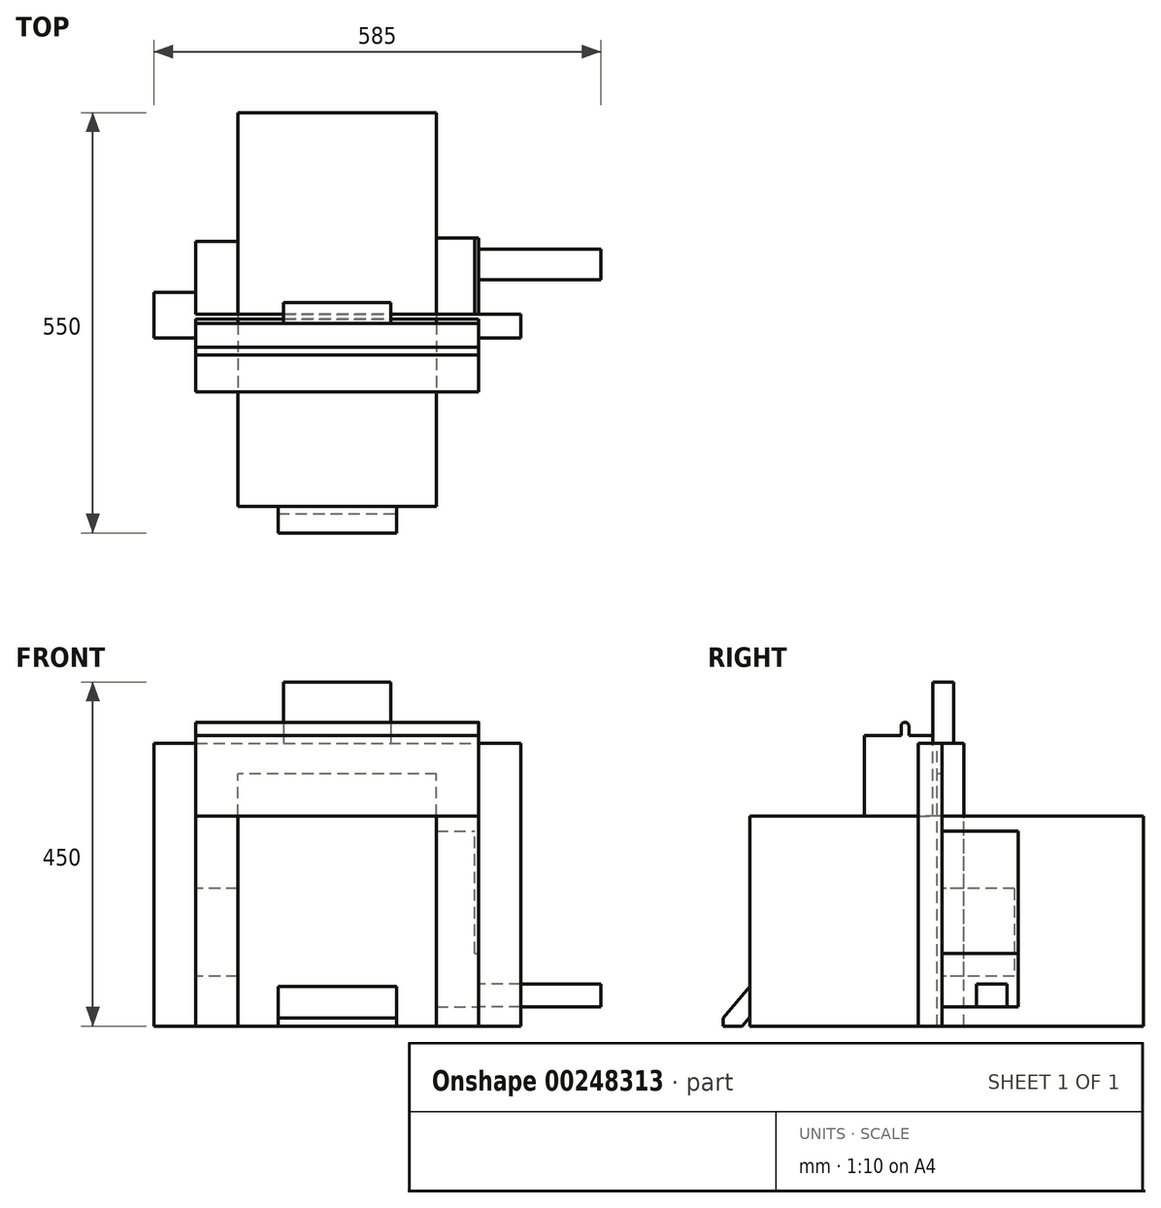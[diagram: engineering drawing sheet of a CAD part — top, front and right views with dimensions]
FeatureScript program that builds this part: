
annotation { "Feature Type Name" : "Feature", "Feature Type Description" : "" }
export const myFeature = defineFeature(function(context is Context, id is Id, definition is map)
    precondition{}
    {
        {
            var Q0;
            Q0=qCreatedBy(makeId("Front.planeOp"),FACE);
            var sketch = newSketch(context, id + "F0", { "sketchPlane" : qUnion([Q0])});
            skLineSegment(sketch, "E0.bottom", {"start": v(-77.5, 0) * mm, "end": v(77.5, 0) * mm});
            skLineSegment(sketch, "E0.top", {"start": v(-77.5, 52) * mm, "end": v(77.5, 52) * mm});
            skLineSegment(sketch, "E0.left", {"start": v(-77.5, 0) * mm, "end": v(-77.5, 52) * mm});
            skLineSegment(sketch, "E0.right", {"start": v(77.5, 0) * mm, "end": v(77.5, 52) * mm});
            skLineSegment(sketch, "E1", {"start": v(0, 0) * mm, "end": v(0, 105.65) * mm, "construction": true});
            skSolve(sketch);
        }
        {
            var Q0;
            Q0 = qSketchRegion(id + "F0", true);
            extrude(context, id + "F1", {"entities" : qUnion([Q0]), "oppositeDirection" : true, "depth" : 65 * mm});
        }
        {
            var Q0;
            Q0=makeQuery(id+"F1.opExtrude","CAP_EDGE",EDGE,{"disambiguationData":[OSD([sQuery(id+"F0.wireOp",EDGE,"E0.top")])],"isStart":true});
            chamfer(context, id + "F2", {"entities" : qUnion([Q0]), "chamferType" : ChamferType.OFFSET_ANGLE, "width" : 35 * mm, "oppositeDirection" : false, "angle" : 50 * degree, "tangentPropagation" : true});
        }
        {
            var Q0;
            Q0=makeQuery(id+"F1.opExtrude","CAP_EDGE",EDGE,{"disambiguationData":[OSD([sQuery(id+"F0.wireOp",EDGE,"E0.bottom")])],"isStart":false});
            chamfer(context, id + "F3", {"entities" : qUnion([Q0]), "chamferType" : ChamferType.OFFSET_ANGLE, "width" : 40 * mm, "oppositeDirection" : false, "angle" : 50 * degree, "tangentPropagation" : true});
        }
        {
            var Q0;
            Q0=makeQuery(id+"F1.opExtrude","SWEPT_FACE",FACE,{"disambiguationData":[OSD([sQuery(id+"F0.wireOp",EDGE,"E0.left")])]});
            var sketch = newSketch(context, id + "F4", { "sketchPlane" : qUnion([Q0])});
            skLineSegment(sketch, "E2.bottom", {"start": v(-35, 52) * mm, "end": v(-95.44, 52) * mm});
            skLineSegment(sketch, "E2.top", {"start": v(-35, 0) * mm, "end": v(-95.44, 0) * mm});
            skLineSegment(sketch, "E2.left", {"start": v(-35, 52) * mm, "end": v(-35, 0) * mm});
            skLineSegment(sketch, "E2.right", {"start": v(-95.44, 52) * mm, "end": v(-95.44, 0) * mm});
            skSolve(sketch);
        }
        {
            var Q0;
            Q0 = qSketchRegion(id + "F4", true);
            extrude(context, id + "F5", {"entities" : qUnion([Q0]), "operationType" : NewBodyOperationType.REMOVE, "endBound" : BoundingType.THROUGH_ALL, "oppositeDirection" : true, "depth" : 25 * mm});
        }
        {
            var Q0;
            Q0=makeQuery(id+"F5.boolean.opBoolean","COPY",FACE,{"derivedFrom":makeQuery(id+"F5.opExtrude","SWEPT_FACE",FACE,{"disambiguationData":[OSD([sQuery(id+"F4.wireOp",EDGE,"E2.left")])]})});
            var sketch = newSketch(context, id + "F6", { "sketchPlane" : qUnion([Q0])});
            skLineSegment(sketch, "E3", {"start": v(0, 0) * mm, "end": v(0, 207.2) * mm, "construction": true});
            skLineSegment(sketch, "E4.bottom", {"start": v(130, 0) * mm, "end": v(-130, 0) * mm});
            skLineSegment(sketch, "E4.top", {"start": v(130, 75) * mm, "end": v(-130, 75) * mm});
            skLineSegment(sketch, "E4.left", {"start": v(130, 0) * mm, "end": v(130, 75) * mm});
            skLineSegment(sketch, "E4.right", {"start": v(-130, 0) * mm, "end": v(-130, 75) * mm});
            skSolve(sketch);
        }
        {
            var Q0;
            Q0 = qSketchRegion(id + "F6", true);
            extrude(context, id + "F7", {"entities" : qUnion([Q0]), "operationType" : NewBodyOperationType.ADD, "depth" : (200 + 235) * mm});
        }
        {
            var Q0;
            Q0=makeQuery(id+"F7.opExtrude","SWEPT_FACE",FACE,{"disambiguationData":[OSD([sQuery(id+"F6.wireOp",EDGE,"E4.left")])]});
            var sketch = newSketch(context, id + "F8", { "sketchPlane" : qUnion([Q0])});
            skLineSegment(sketch, "E5.0", {"start": v(-280, 0) * mm, "end": v(-280, 370) * mm});
            skLineSegment(sketch, "E6.0", {"start": v(-286.3, 0) * mm, "end": v(-286.3, 370) * mm});
            skLineSegment(sketch, "E7", {"start": v(-286.3, 370) * mm, "end": v(-280, 370) * mm});
            skLineSegment(sketch, "E8", {"start": v(-280, 0) * mm, "end": v(-286.3, 0) * mm});
            skSolve(sketch);
        }
        {
            var Q0;
            Q0 = qSketchRegion(id + "F8", true);
            extrude(context, id + "F9", {"entities" : qUnion([Q0]), "operationType" : NewBodyOperationType.ADD, "depth" : 55 * mm});
        }
        {
            var Q0;
            Q0=makeQuery(id+"F9.opExtrude","CAP_FACE",FACE,{"disambiguationData":[OSD([sQuery(id+"F8.wireOp",EDGE,"E5.0"),sQuery(id+"F8.wireOp",EDGE,"E6.0"),sQuery(id+"F8.wireOp",EDGE,"E7"),sQuery(id+"F8.wireOp",EDGE,"E8")])],"isStart":true});
            var sketch = newSketch(context, id + "F10", { "sketchPlane" : qUnion([Q0])});
            skLineSegment(sketch, "E9.0", {"start": v(286.3, 370) * mm, "end": v(280, 370) * mm});
            skLineSegment(sketch, "E10.0", {"start": v(286.3, 329.7) * mm, "end": v(280, 329.7) * mm});
            skLineSegment(sketch, "E11", {"start": v(280, 370) * mm, "end": v(280, 329.7) * mm});
            skLineSegment(sketch, "E12", {"start": v(286.3, 370) * mm, "end": v(286.3, 329.7) * mm});
            skSolve(sketch);
        }
        {
            var Q0;
            Q0 = qSketchRegion(id + "F10", true);
            extrude(context, id + "F11", {"entities" : qUnion([Q0]), "operationType" : NewBodyOperationType.ADD, "depth" : 260 * mm});
        }
        {
            var Q0;
            Q0=makeQuery(id+"F11.boolean.opBoolean","MERGE",FACE,{"derivedFrom":[makeQuery(id+"F9.opExtrude","SWEPT_FACE",FACE,{"disambiguationData":[OSD([sQuery(id+"F8.wireOp",EDGE,"E5.0")])]}),makeQuery(id+"F11.opExtrude","SWEPT_FACE",FACE,{"disambiguationData":[OSD([sQuery(id+"F10.wireOp",EDGE,"E11")])]})]});
            var sketch = newSketch(context, id + "F12", { "sketchPlane" : qUnion([Q0])});
            skLineSegment(sketch, "E13.0", {"start": v(130, 0) * mm, "end": v(130, 370) * mm});
            skLineSegment(sketch, "E14.0", {"start": v(185, 0) * mm, "end": v(185, 370) * mm});
            skLineSegment(sketch, "E15", {"start": v(130, 370) * mm, "end": v(185, 370) * mm});
            skLineSegment(sketch, "E16", {"start": v(130, 0) * mm, "end": v(185, 0) * mm});
            skSolve(sketch);
        }
        {
            var Q0;
            Q0 = qSketchRegion(id + "F12", true);
            extrude(context, id + "F13", {"entities" : qUnion([Q0]), "operationType" : NewBodyOperationType.ADD, "oppositeDirection" : true, "depth" : 6.3 * mm});
        }
        {
            var Q0;
            Q0=makeQuery(id+"F9.opExtrude","CAP_FACE",FACE,{"disambiguationData":[OSD([sQuery(id+"F8.wireOp",EDGE,"E5.0"),sQuery(id+"F8.wireOp",EDGE,"E6.0"),sQuery(id+"F8.wireOp",EDGE,"E7"),sQuery(id+"F8.wireOp",EDGE,"E8")])],"isStart":false});
            var sketch = newSketch(context, id + "F14", { "sketchPlane" : qUnion([Q0])});
            skLineSegment(sketch, "E17.0", {"start": v(-381.3, 65) * mm, "end": v(-286.3, 65) * mm});
            skLineSegment(sketch, "E18.0", {"start": v(-381.3, 180) * mm, "end": v(-286.3, 180) * mm});
            skLineSegment(sketch, "E19", {"start": v(-381.3, 180) * mm, "end": v(-381.3, 65) * mm});
            skLineSegment(sketch, "E20", {"start": v(-286.3, 180) * mm, "end": v(-286.3, 65) * mm});
            skSolve(sketch);
        }
        {
            var Q0;
            Q0 = qSketchRegion(id + "F14", true);
            extrude(context, id + "F15", {"entities" : qUnion([Q0]), "operationType" : NewBodyOperationType.ADD, "oppositeDirection" : true, "depth" : 55 * mm});
        }
        {
            var Q0;
            Q0=makeQuery(id+"F13.opExtrude","SWEPT_FACE",FACE,{"disambiguationData":[OSD([sQuery(id+"F12.wireOp",EDGE,"E14.0")])]});
            var sketch = newSketch(context, id + "F16", { "sketchPlane" : qUnion([Q0])});
            skLineSegment(sketch, "E21.0", {"start": v(386.3, 25) * mm, "end": v(286.3, 25) * mm});
            skLineSegment(sketch, "E22.0", {"start": v(386.3, 255) * mm, "end": v(286.3, 255) * mm});
            skLineSegment(sketch, "E23", {"start": v(386.3, 255) * mm, "end": v(386.3, 25) * mm});
            skLineSegment(sketch, "E24", {"start": v(286.3, 255) * mm, "end": v(286.3, 25) * mm});
            skSolve(sketch);
        }
        {
            var Q0;
            Q0 = qSketchRegion(id + "F16", true);
            extrude(context, id + "F17", {"entities" : qUnion([Q0]), "operationType" : NewBodyOperationType.ADD, "oppositeDirection" : true, "depth" : 55 * mm});
        }
        {
            var Q0;
            Q0=makeQuery(id+"F7.opExtrude","CAP_FACE",FACE,{"disambiguationData":[OSD([sQuery(id+"F6.wireOp",EDGE,"E4.bottom"),sQuery(id+"F6.wireOp",EDGE,"E4.top"),sQuery(id+"F6.wireOp",EDGE,"E4.left"),sQuery(id+"F6.wireOp",EDGE,"E4.right")])],"isStart":false});
            var sketch = newSketch(context, id + "F18", { "sketchPlane" : qUnion([Q0])});
            skSolve(sketch);
        }
        {
            var Q0;
            Q0=makeQuery(id+"F18.imprint","IMPRINT",FACE,{"disambiguationData":[TD([[makeQuery(id+"F18.imprint","IMPRINT",EDGE,{"derivedFrom":makeQuery(id+"F7.opExtrude","CAP_EDGE",EDGE,{"disambiguationData":[OSD([sQuery(id+"F6.wireOp",EDGE,"E4.bottom")])],"isStart":false})}),-1.0]])]});
            extrude(context, id + "F19", {"entities" : qUnion([Q0]), "operationType" : NewBodyOperationType.ADD, "depth" : 80 * mm});
        }
        {
            var Q0;
            Q0=makeQuery(id+"F17.boolean.opBoolean","MERGE",FACE,{"derivedFrom":[makeQuery(id+"F13.opExtrude","SWEPT_FACE",FACE,{"disambiguationData":[OSD([sQuery(id+"F12.wireOp",EDGE,"E14.0")])]}),makeQuery(id+"F17.opExtrude","CAP_FACE",FACE,{"disambiguationData":[OSD([sQuery(id+"F16.wireOp",EDGE,"E21.0"),sQuery(id+"F16.wireOp",EDGE,"E22.0"),sQuery(id+"F16.wireOp",EDGE,"E23"),sQuery(id+"F16.wireOp",EDGE,"E24")])],"isStart":true})]});
            var sketch = newSketch(context, id + "F20", { "sketchPlane" : qUnion([Q0])});
            skLineSegment(sketch, "E25.0", {"start": v(371.3, 55) * mm, "end": v(371.3, 25) * mm});
            skLineSegment(sketch, "E26", {"start": v(286.3, 25) * mm, "end": v(286.3, 255) * mm, "construction": true});
            skLineSegment(sketch, "E27.0", {"start": v(331.3, 25) * mm, "end": v(331.3, 55) * mm});
            skLineSegment(sketch, "E28", {"start": v(331.3, 55) * mm, "end": v(371.3, 55) * mm});
            skLineSegment(sketch, "E29", {"start": v(331.3, 25) * mm, "end": v(371.3, 25) * mm});
            skSolve(sketch);
        }
        {
            var Q0;
            Q0 = qSketchRegion(id + "F20", true);
            extrude(context, id + "F21", {"entities" : qUnion([Q0]), "operationType" : NewBodyOperationType.ADD, "depth" : 60 * mm});
        }
        {
            var Q0;
            Q0=makeQuery(id+"F15.boolean.opBoolean","MERGE",FACE,{"derivedFrom":[makeQuery(id+"F9.opExtrude","CAP_FACE",FACE,{"disambiguationData":[OSD([sQuery(id+"F8.wireOp",EDGE,"E5.0"),sQuery(id+"F8.wireOp",EDGE,"E6.0"),sQuery(id+"F8.wireOp",EDGE,"E7"),sQuery(id+"F8.wireOp",EDGE,"E8")])],"isStart":false}),makeQuery(id+"F15.opExtrude","CAP_FACE",FACE,{"disambiguationData":[OSD([sQuery(id+"F14.wireOp",EDGE,"E17.0"),sQuery(id+"F14.wireOp",EDGE,"E18.0"),sQuery(id+"F14.wireOp",EDGE,"E19"),sQuery(id+"F14.wireOp",EDGE,"E20")])],"isStart":true})]});
            var sketch = newSketch(context, id + "F22", { "sketchPlane" : qUnion([Q0])});
            skLineSegment(sketch, "E30.0", {"start": v(-255, 0) * mm, "end": v(-255, 370) * mm});
            skLineSegment(sketch, "E31.0", {"start": v(-315, 0) * mm, "end": v(-315, 370) * mm});
            skLineSegment(sketch, "E32", {"start": v(-315, 370) * mm, "end": v(-255, 370) * mm});
            skLineSegment(sketch, "E33", {"start": v(-315, 0) * mm, "end": v(-255, 0) * mm});
            skSolve(sketch);
        }
        {
            var Q0;
            Q0 = qSketchRegion(id + "F22", true);
            extrude(context, id + "F23", {"entities" : qUnion([Q0]), "operationType" : NewBodyOperationType.ADD, "depth" : 55 * mm});
        }
        {
            var Q0;
            Q0=makeQuery(id+"F17.boolean.opBoolean","MERGE",FACE,{"derivedFrom":[makeQuery(id+"F13.opExtrude","SWEPT_FACE",FACE,{"disambiguationData":[OSD([sQuery(id+"F12.wireOp",EDGE,"E14.0")])]}),makeQuery(id+"F17.opExtrude","CAP_FACE",FACE,{"disambiguationData":[OSD([sQuery(id+"F16.wireOp",EDGE,"E21.0"),sQuery(id+"F16.wireOp",EDGE,"E22.0"),sQuery(id+"F16.wireOp",EDGE,"E23"),sQuery(id+"F16.wireOp",EDGE,"E24")])],"isStart":true})]});
            var sketch = newSketch(context, id + "F24", { "sketchPlane" : qUnion([Q0])});
            skLineSegment(sketch, "E34.0", {"start": v(255, 0) * mm, "end": v(255, 370) * mm});
            skLineSegment(sketch, "E35.0", {"start": v(315, 0) * mm, "end": v(315, 370) * mm});
            skLineSegment(sketch, "E36.0", {"start": v(315, 370) * mm, "end": v(255, 370) * mm});
            skLineSegment(sketch, "E37.0", {"start": v(315, 0) * mm, "end": v(255, 0) * mm});
            skSolve(sketch);
        }
        {
            var Q0;
            Q0 = qSketchRegion(id + "F24", true);
            extrude(context, id + "F25", {"entities" : qUnion([Q0]), "operationType" : NewBodyOperationType.ADD, "depth" : 55 * mm});
        }
        {
            var Q0;
            Q0=makeQuery(id+"F25.opExtrude","CAP_FACE",FACE,{"disambiguationData":[OSD([sQuery(id+"F24.wireOp",EDGE,"E34.0"),sQuery(id+"F24.wireOp",EDGE,"E35.0"),sQuery(id+"F24.wireOp",EDGE,"E36.0"),sQuery(id+"F24.wireOp",EDGE,"E37.0")])],"isStart":false});
            var sketch = newSketch(context, id + "F26", { "sketchPlane" : qUnion([Q0])});
            skLineSegment(sketch, "E38.0", {"start": v(315, 25) * mm, "end": v(315, 255) * mm});
            skLineSegment(sketch, "E39.0", {"start": v(286.3, 255) * mm, "end": v(286.3, 370) * mm});
            skLineSegment(sketch, "E40", {"start": v(286.3, 370) * mm, "end": v(315, 370) * mm});
            skLineSegment(sketch, "E41", {"start": v(315, 25) * mm, "end": v(315, 0) * mm});
            skLineSegment(sketch, "E42", {"start": v(315, 0) * mm, "end": v(286.3, 0) * mm});
            skLineSegment(sketch, "E43", {"start": v(315, 255) * mm, "end": v(315, 370) * mm});
            skLineSegment(sketch, "E44", {"start": v(286.3, 255) * mm, "end": v(286.3, 0) * mm});
            skSolve(sketch);
        }
        {
            var Q0;
            Q0 = qSketchRegion(id + "F26", true);
            extrude(context, id + "F27", {"entities" : qUnion([Q0]), "operationType" : NewBodyOperationType.REMOVE, "oppositeDirection" : true, "depth" : 55 * mm});
        }
        {
            var Q0;
            {var subQ0=sQuery(id+"F6.wireOp",EDGE,"E4.top");Q0=makeQuery(id+"F19.boolean.opBoolean","MERGE",FACE,{"derivedFrom":[makeQuery(id+"F7.opExtrude","SWEPT_FACE",FACE,{"disambiguationData":[OSD([subQ0])]}),makeQuery(id+"F19.opExtrude","SWEPT_FACE",FACE,{"disambiguationData":[OSD([subQ0])]})]});}
            var sketch = newSketch(context, id + "F28", { "sketchPlane" : qUnion([Q0])});
            skSolve(sketch);
        }
        {
            var Q0;
            {var subQ7=sQuery(id+"F6.wireOp",EDGE,"E4.top");Q0=makeQuery(id+"F28.imprint","IMPRINT",FACE,{"disambiguationData":[TD([[makeQuery(id+"F28.imprint","IMPRINT",EDGE,{"derivedFrom":makeQuery(id+"F7.opExtrude","CAP_EDGE",EDGE,{"disambiguationData":[OSD([subQ7])],"isStart":true})}),1.0]])]});}
            extrude(context, id + "F29", {"entities" : qUnion([Q0]), "operationType" : NewBodyOperationType.ADD, "depth" : 200 * mm});
        }
        {
            var Q0;
            Q0=makeQuery(id+"F13.boolean.opBoolean","MERGE",FACE,{"derivedFrom":[makeQuery(id+"F11.boolean.opBoolean","MERGE",FACE,{"derivedFrom":[makeQuery(id+"F9.opExtrude","SWEPT_FACE",FACE,{"disambiguationData":[OSD([sQuery(id+"F8.wireOp",EDGE,"E5.0")])]}),makeQuery(id+"F11.opExtrude","SWEPT_FACE",FACE,{"disambiguationData":[OSD([sQuery(id+"F10.wireOp",EDGE,"E11")])]})]}),makeQuery(id+"F13.opExtrude","CAP_FACE",FACE,{"disambiguationData":[OSD([sQuery(id+"F12.wireOp",EDGE,"E13.0"),sQuery(id+"F12.wireOp",EDGE,"E14.0"),sQuery(id+"F12.wireOp",EDGE,"E15"),sQuery(id+"F12.wireOp",EDGE,"E16")])],"isStart":true})]});
            var sketch = newSketch(context, id + "F30", { "sketchPlane" : qUnion([Q0])});
            skLineSegment(sketch, "E45.0", {"start": v(-185, 380) * mm, "end": v(185, 380) * mm});
            skLineSegment(sketch, "E46", {"start": v(-130, 275) * mm, "end": v(299.39, 275) * mm, "construction": true});
            skLineSegment(sketch, "E47", {"start": v(185, 380) * mm, "end": v(185, 275) * mm});
            skLineSegment(sketch, "E48", {"start": v(185, 275) * mm, "end": v(-185, 275) * mm});
            skLineSegment(sketch, "E49", {"start": v(-185, 275) * mm, "end": v(-185, 380) * mm});
            skSolve(sketch);
        }
        {
            var Q0;
            Q0 = qSketchRegion(id + "F30", true);
            extrude(context, id + "F31", {"entities" : qUnion([Q0]), "depth" : 95 * mm});
        }
        {
            var Q0;
            Q0=makeQuery(id+"F31.opExtrude","SWEPT_FACE",FACE,{"disambiguationData":[OSD([sQuery(id+"F30.wireOp",EDGE,"E45.0")])]});
            var sketch = newSketch(context, id + "F32", { "sketchPlane" : qUnion([Q0])});
            skLineSegment(sketch, "E50.0", {"start": v(-185, 243) * mm, "end": v(185, 243) * mm});
            skLineSegment(sketch, "E51.0", {"start": v(-185, 233) * mm, "end": v(185, 233) * mm});
            skLineSegment(sketch, "E52", {"start": v(185, 243) * mm, "end": v(185, 233) * mm});
            skLineSegment(sketch, "E53", {"start": v(-185, 243) * mm, "end": v(-185, 233) * mm});
            skSolve(sketch);
        }
        {
            var Q0;
            Q0 = qSketchRegion(id + "F32", true);
            extrude(context, id + "F33", {"entities" : qUnion([Q0]), "operationType" : NewBodyOperationType.ADD, "depth" : 17.5 * mm});
        }
        {
            var Q0;
            Q0=makeQuery(id+"F33.opExtrude","CAP_EDGE",EDGE,{"disambiguationData":[OSD([sQuery(id+"F32.wireOp",EDGE,"E51.0")])],"isStart":false});
            var Q1;
            Q1=makeQuery(id+"F33.opExtrude","CAP_EDGE",EDGE,{"disambiguationData":[OSD([sQuery(id+"F32.wireOp",EDGE,"E50.0")])],"isStart":false});
            fillet(context, id + "F34", {"entities" : qUnion([Q0, Q1]), "radius" : 5 * mm, "tangentPropagation" : true, "allowEdgeOverflow" : false});
        }
        {
            var Q0;
            {var subQ2=sQuery(id+"F30.wireOp",EDGE,"E45.0");Q0=makeQuery(id+"F33.boolean.opBoolean","SPLIT",FACE,{"disambiguationData":[TD([makeQuery(id+"F33.opExtrude","SWEPT_FACE",FACE,{"disambiguationData":[OSD([sQuery(id+"F32.wireOp",EDGE,"E50.0")])]})])],"derivedFrom":makeQuery(id+"F31.opExtrude","SWEPT_FACE",FACE,{"disambiguationData":[OSD([subQ2])]})});}
            var sketch = newSketch(context, id + "F35", { "sketchPlane" : qUnion([Q0])});
            skLineSegment(sketch, "E54.0", {"start": v(-185, 274.5) * mm, "end": v(185, 274.5) * mm});
            skLineSegment(sketch, "E55", {"start": v(-185, 274.5) * mm, "end": v(-185, 280) * mm});
            skLineSegment(sketch, "E56", {"start": v(-185, 280) * mm, "end": v(185, 280) * mm});
            skLineSegment(sketch, "E57", {"start": v(185, 280) * mm, "end": v(185, 274.5) * mm});
            skSolve(sketch);
        }
        {
            var Q0;
            Q0 = qSketchRegion(id + "F35", true);
            extrude(context, id + "F36", {"entities" : qUnion([Q0]), "operationType" : NewBodyOperationType.REMOVE, "oppositeDirection" : true, "depth" : 105 * mm});
        }
        {
            var Q0;
            Q0=makeQuery(id+"F25.boolean.opBoolean","MERGE",FACE,{"derivedFrom":[makeQuery(id+"F23.boolean.opBoolean","MERGE",FACE,{"derivedFrom":[makeQuery(id+"F13.boolean.opBoolean","MERGE",FACE,{"derivedFrom":[makeQuery(id+"F11.boolean.opBoolean","MERGE",FACE,{"derivedFrom":[makeQuery(id+"F9.opExtrude","SWEPT_FACE",FACE,{"disambiguationData":[OSD([sQuery(id+"F8.wireOp",EDGE,"E7")])]}),makeQuery(id+"F11.opExtrude","SWEPT_FACE",FACE,{"disambiguationData":[OSD([sQuery(id+"F10.wireOp",EDGE,"E9.0")])]})]}),makeQuery(id+"F13.opExtrude","SWEPT_FACE",FACE,{"disambiguationData":[OSD([sQuery(id+"F12.wireOp",EDGE,"E15")])]})]}),makeQuery(id+"F23.opExtrude","SWEPT_FACE",FACE,{"disambiguationData":[OSD([sQuery(id+"F22.wireOp",EDGE,"E32")])]})]}),makeQuery(id+"F25.opExtrude","SWEPT_FACE",FACE,{"disambiguationData":[OSD([sQuery(id+"F24.wireOp",EDGE,"E36.0")])]})]});
            var sketch = newSketch(context, id + "F37", { "sketchPlane" : qUnion([Q0])});
            skLineSegment(sketch, "E58", {"start": v(0, 280) * mm, "end": v(0, 286.3) * mm});
            skLineSegment(sketch, "E59.0", {"start": v(-185, 274.5) * mm, "end": v(185, 274.5) * mm, "construction": true});
            skLineSegment(sketch, "E60.bottom", {"start": v(-70, 274.5) * mm, "end": v(70, 274.5) * mm});
            skLineSegment(sketch, "E60.top", {"start": v(-70, 301.5) * mm, "end": v(70, 301.5) * mm});
            skLineSegment(sketch, "E60.left", {"start": v(-70, 274.5) * mm, "end": v(-70, 301.5) * mm});
            skLineSegment(sketch, "E60.right", {"start": v(70, 274.5) * mm, "end": v(70, 301.5) * mm});
            skSolve(sketch);
        }
        {
            var Q0;
            Q0 = qSketchRegion(id + "F37", true);
            extrude(context, id + "F38", {"entities" : qUnion([Q0]), "depth" : 80 * mm});
        }
        {
            var Q0;
            Q0=makeQuery(id+"F21.opExtrude","CAP_FACE",FACE,{"disambiguationData":[OSD([sQuery(id+"F20.wireOp",EDGE,"E25.0"),sQuery(id+"F20.wireOp",EDGE,"E27.0"),sQuery(id+"F20.wireOp",EDGE,"E28"),sQuery(id+"F20.wireOp",EDGE,"E29")])],"isStart":false});
            extrude(context, id + "F39", {"entities" : qUnion([Q0]), "operationType" : NewBodyOperationType.ADD, "depth" : 100 * mm});
        }
        {
            var Q0;
            Q0=makeQuery(id+"F27.boolean.opBoolean","MERGE",FACE,{"derivedFrom":[makeQuery(id+"F17.boolean.opBoolean","MERGE",FACE,{"derivedFrom":[makeQuery(id+"F13.opExtrude","SWEPT_FACE",FACE,{"disambiguationData":[OSD([sQuery(id+"F12.wireOp",EDGE,"E14.0")])]}),makeQuery(id+"F17.opExtrude","CAP_FACE",FACE,{"disambiguationData":[OSD([sQuery(id+"F16.wireOp",EDGE,"E21.0"),sQuery(id+"F16.wireOp",EDGE,"E22.0"),sQuery(id+"F16.wireOp",EDGE,"E23"),sQuery(id+"F16.wireOp",EDGE,"E24")])],"isStart":true})]}),makeQuery(id+"F27.opExtrude","CAP_FACE",FACE,{"disambiguationData":[OSD([sQuery(id+"F26.wireOp",EDGE,"E38.0"),sQuery(id+"F26.wireOp",EDGE,"E39.0"),sQuery(id+"F26.wireOp",EDGE,"E40"),sQuery(id+"F26.wireOp",EDGE,"E41"),sQuery(id+"F26.wireOp",EDGE,"E42"),sQuery(id+"F26.wireOp",EDGE,"E43"),sQuery(id+"F26.wireOp",EDGE,"E44")])],"isStart":false})]});
            var sketch = newSketch(context, id + "F40", { "sketchPlane" : qUnion([Q0])});
            skLineSegment(sketch, "E61", {"start": v(286.3, 95) * mm, "end": v(386.3, 95) * mm});
            skLineSegment(sketch, "E62", {"start": v(386.3, 95) * mm, "end": v(386.3, 255) * mm});
            skLineSegment(sketch, "E63", {"start": v(386.3, 255) * mm, "end": v(286.3, 255) * mm});
            skLineSegment(sketch, "E64", {"start": v(286.3, 255) * mm, "end": v(286.3, 95) * mm});
            skSolve(sketch);
        }
        {
            var Q0;
            Q0=makeQuery(id+"F40.imprint","IMPRINT",FACE,{"disambiguationData":[TD([[makeQuery(id+"F40.imprint","IMPRINT",EDGE,{"derivedFrom":sQuery(id+"F40.wireOp",EDGE,"E61")}),1.0]])]});
            extrude(context, id + "F41", {"entities" : qUnion([Q0]), "operationType" : NewBodyOperationType.REMOVE, "oppositeDirection" : true, "depth" : 5 * mm});
        }
    });
